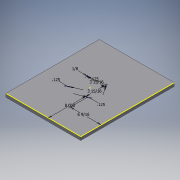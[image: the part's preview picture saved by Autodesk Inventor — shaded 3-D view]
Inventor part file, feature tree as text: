
AUTODESK INVENTOR PART (.ipt)
format: ipt  version: 2016 (Build 200138000, 138)  size: 101,376 bytes
history: native  units: in
note: dims shown in document units (in); Inventor stores cm internally (conversion verified against a paired STEP export)
features: sketch x2, extrude x1
ambient origin geometry x8: Origin, YZ Plane, XZ Plane, XY Plane, X Axis, Y Axis, Z Axis, Center Point
bodies: Solid1 (feature_tree)
feature tree (3):
  extrude  "Extrusion1"  Depth=20.0in
  sketch  "Sketch2"  dims[d2=0.75in d3=0.0in d4=6.5625in d5=8.0in d6=3.9375in d7=3.9375in d9=0.125in d10=0.125in d11=0.125in d12=0.125in]
  sketch  "Sketch1"  dims[d0=16.0in d1=20.0in]
